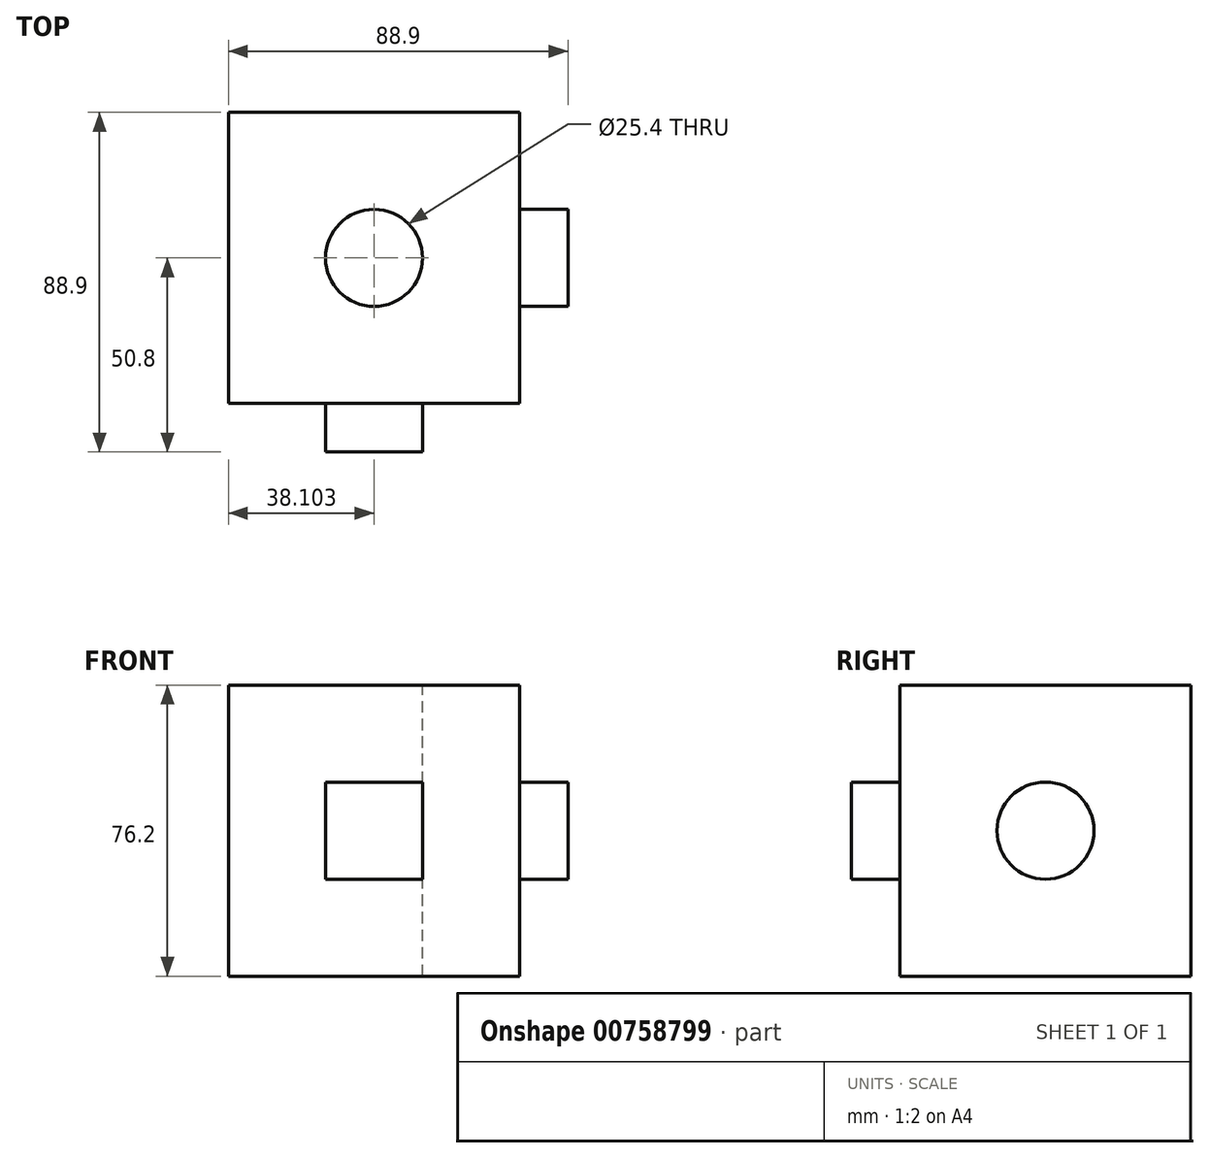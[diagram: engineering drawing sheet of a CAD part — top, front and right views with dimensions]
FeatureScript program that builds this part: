
annotation { "Feature Type Name" : "Feature", "Feature Type Description" : "" }
export const myFeature = defineFeature(function(context is Context, id is Id, definition is map)
    precondition{}
    {
        {
            var Q0;
            Q0=qCreatedBy(makeId("Front.planeOp"),FACE);
            var sketch = newSketch(context, id + "F0", { "sketchPlane" : qUnion([Q0])});
            skLineSegment(sketch, "E0.bottom", {"start": v(-55.99, 0) * mm, "end": v(20.21, 0) * mm});
            skLineSegment(sketch, "E0.top", {"start": v(-55.99, 76.2) * mm, "end": v(20.21, 76.2) * mm});
            skLineSegment(sketch, "E0.left", {"start": v(-55.99, 0) * mm, "end": v(-55.99, 76.2) * mm});
            skLineSegment(sketch, "E0.right", {"start": v(20.21, 0) * mm, "end": v(20.21, 76.2) * mm});
            skSolve(sketch);
        }
        {
            var Q0;
            Q0=makeQuery(id+"F0.imprint","IMPRINT",FACE,{"disambiguationData":[TD([[makeQuery(id+"F0.imprint","IMPRINT",EDGE,{"derivedFrom":sQuery(id+"F0.wireOp",EDGE,"E0.bottom")}),1.0]])]});
            extrude(context, id + "F1", {"entities" : qUnion([Q0]), "depth" : 76.2 * mm, "offsetDistance" : 25.4 * mm});
        }
        {
            var Q0;
            Q0=makeQuery(id+"F1.opExtrude","CAP_FACE",FACE,{"disambiguationData":[OSD([sQuery(id+"F0.wireOp",EDGE,"E0.bottom"),sQuery(id+"F0.wireOp",EDGE,"E0.top"),sQuery(id+"F0.wireOp",EDGE,"E0.left"),sQuery(id+"F0.wireOp",EDGE,"E0.right")])],"isStart":false});
            var sketch = newSketch(context, id + "F2", { "sketchPlane" : qUnion([Q0])});
            skLineSegment(sketch, "E1.bottom", {"start": v(-30.59, 50.8) * mm, "end": v(-5.19, 50.8) * mm});
            skLineSegment(sketch, "E1.top", {"start": v(-30.59, 25.4) * mm, "end": v(-5.19, 25.4) * mm});
            skLineSegment(sketch, "E1.left", {"start": v(-30.59, 50.8) * mm, "end": v(-30.59, 25.4) * mm});
            skLineSegment(sketch, "E1.right", {"start": v(-5.19, 50.8) * mm, "end": v(-5.19, 25.4) * mm});
            skSolve(sketch);
        }
        {
            var Q0;
            Q0=makeQuery(id+"F2.imprint","IMPRINT",FACE,{"disambiguationData":[TD([[makeQuery(id+"F2.imprint","IMPRINT",EDGE,{"derivedFrom":sQuery(id+"F2.wireOp",EDGE,"E1.bottom")}),-1.0]])]});
            extrude(context, id + "F3", {"entities" : qUnion([Q0]), "operationType" : NewBodyOperationType.ADD, "depth" : 12.7 * mm, "offsetDistance" : 25.4 * mm});
        }
        {
            var Q0;
            Q0=makeQuery(id+"F1.opExtrude","SWEPT_FACE",FACE,{"disambiguationData":[OSD([sQuery(id+"F0.wireOp",EDGE,"E0.right")])]});
            var sketch = newSketch(context, id + "F4", { "sketchPlane" : qUnion([Q0])});
            skSolve(sketch);
        }
        {
            var Q0;
            {var subQ0=sQuery(id+"F0.wireOp",EDGE,"E0.right");Q0=makeQuery(id+"F4.imprint","IMPRINT",FACE,{"disambiguationData":[TD([[makeQuery(id+"F4.imprint","IMPRINT",EDGE,{"derivedFrom":makeQuery(id+"F1.opExtrude","CAP_EDGE",EDGE,{"disambiguationData":[OSD([subQ0])],"isStart":true})}),1.0]])]});}
            var sketch = newSketch(context, id + "F5", { "sketchPlane" : qUnion([Q0])});
            skCircle(sketch, "E2", {"center": v(-38.1, 38.1) * mm, "radius": 12.7 * mm});
            skSolve(sketch);
        }
        {
            var Q0;
            Q0=makeQuery(id+"F5.imprint","IMPRINT",FACE,{"disambiguationData":[TD([[makeQuery(id+"F5.imprint","IMPRINT",EDGE,{"derivedFrom":sQuery(id+"F5.wireOp",EDGE,"E2")}),1.0]])]});
            extrude(context, id + "F6", {"entities" : qUnion([Q0]), "operationType" : NewBodyOperationType.ADD, "depth" : 12.7 * mm, "offsetDistance" : 25.4 * mm});
        }
        {
            var Q0;
            Q0=makeQuery(id+"F1.opExtrude","SWEPT_FACE",FACE,{"disambiguationData":[OSD([sQuery(id+"F0.wireOp",EDGE,"E0.top")])]});
            var sketch = newSketch(context, id + "F7", { "sketchPlane" : qUnion([Q0])});
            skPoint(sketch, "E3", {"position": v(-17.89, -38.1) * mm});
            skSolve(sketch);
        }
        {
            var Q0;
            Q0=sQuery(id+"F7.wireOp",VERTEX,"E3");
            var Q1;
            Q1=makeQuery(id+"F1.opExtrude","SWEPT_BODY",BODY,{"disambiguationData":[OSD([sQuery(id+"F0.wireOp",EDGE,"E0.bottom"),sQuery(id+"F0.wireOp",EDGE,"E0.top"),sQuery(id+"F0.wireOp",EDGE,"E0.left"),sQuery(id+"F0.wireOp",EDGE,"E0.right")])]});
            hole(context, id + "F8", {"style" : HoleStyle.SIMPLE, "endStyle" : HoleEndStyle.THROUGH, "holeDiameter" : 25.4 * mm, "majorDiameter" : 6.35 * mm, "isTappedThrough" : true, "tappedDepth" : 12.7 * mm, "tapClearance" : 3, "locations" : qUnion([Q0]), "scope" : qUnion([Q1])});
        }
    });
